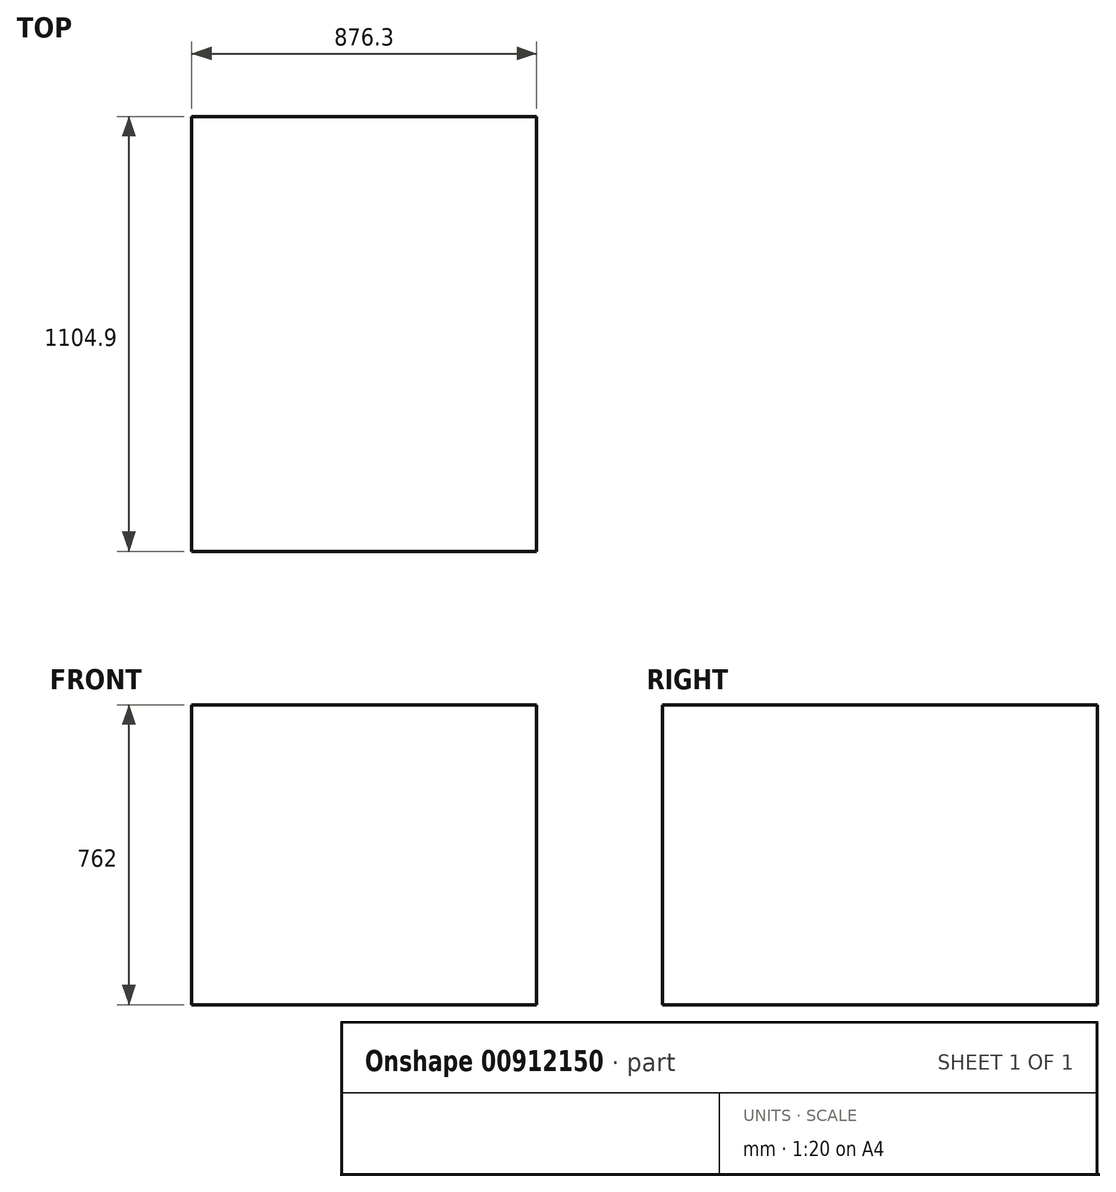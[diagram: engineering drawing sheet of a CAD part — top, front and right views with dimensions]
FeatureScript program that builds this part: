
annotation { "Feature Type Name" : "Feature", "Feature Type Description" : "" }
export const myFeature = defineFeature(function(context is Context, id is Id, definition is map)
    precondition{}
    {
        {
            var Q0;
            Q0=qCreatedBy(makeId("Front.planeOp"),FACE);
            var sketch = newSketch(context, id + "F0", { "sketchPlane" : qUnion([Q0])});
            skLineSegment(sketch, "E0.bottom", {"start": v(-853.18, 721.04) * mm, "end": v(23.12, 721.04) * mm});
            skLineSegment(sketch, "E0.top", {"start": v(-853.18, -40.96) * mm, "end": v(23.12, -40.96) * mm});
            skLineSegment(sketch, "E0.left", {"start": v(-853.18, 721.04) * mm, "end": v(-853.18, -40.96) * mm});
            skLineSegment(sketch, "E0.right", {"start": v(23.12, 721.04) * mm, "end": v(23.12, -40.96) * mm});
            skSolve(sketch);
        }
        {
            var Q0;
            Q0=makeQuery(id+"F0.imprint","IMPRINT",FACE,{"disambiguationData":[TD([[makeQuery(id+"F0.imprint","IMPRINT",EDGE,{"derivedFrom":sQuery(id+"F0.wireOp",EDGE,"E0.bottom")}),-1.0]])]});
            extrude(context, id + "F1", {"entities" : qUnion([Q0]), "oppositeDirection" : true, "depth" : 1104.9 * mm, "offsetDistance" : 25.4 * mm});
        }
    });
